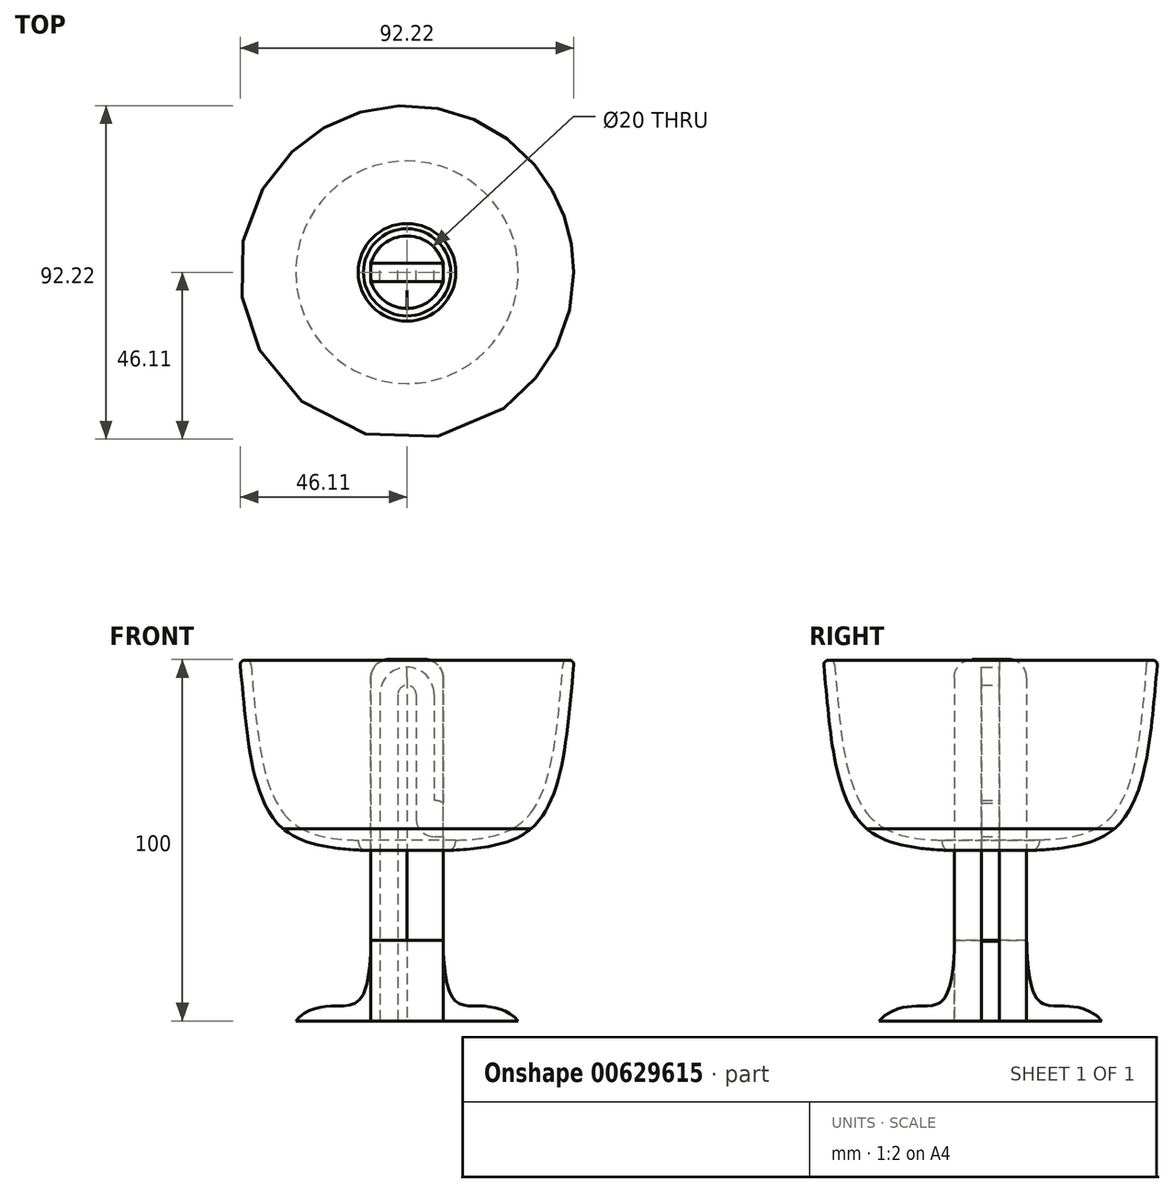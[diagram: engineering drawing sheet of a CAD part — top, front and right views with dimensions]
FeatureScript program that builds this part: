
annotation { "Feature Type Name" : "Feature", "Feature Type Description" : "" }
export const myFeature = defineFeature(function(context is Context, id is Id, definition is map)
    precondition{}
    {
        {
            var Q0;
            Q0=qCreatedBy(makeId("Front.planeOp"),FACE);
            var sketch = newSketch(context, id + "F0", { "sketchPlane" : qUnion([Q0])});
            skLineSegment(sketch, "E0.bottom", {"start": v(10, 50) * mm, "end": v(-10, 50) * mm});
            skLineSegment(sketch, "E0.top", {"start": v(10, -50) * mm, "end": v(-10, -50) * mm});
            skLineSegment(sketch, "E0.left", {"start": v(10, 50) * mm, "end": v(10, -50) * mm});
            skLineSegment(sketch, "E0.right", {"start": v(-10, 50) * mm, "end": v(-10, -50) * mm});
            skPoint(sketch, "E0.middle", {"position": v(0, 0) * mm});
            skLineSegment(sketch, "E1", {"start": v(10, -50) * mm, "end": v(30.79, -50) * mm});
            skFitSpline(sketch, "E2", {"points": [v(30.79, -50) * mm, v(20.87, -45.89) * mm, v(12.34, -43.12) * mm, v(10, -27.67) * mm, v(10, -27.9) * mm], "startDerivative": vector(-25.17, 29.69) * mm, "endDerivative": vector(0.32, -8.68) * mm});
            skFitSpline(sketch, "E3", {"points": [v(10, 0) * mm, v(32.17, 5.3) * mm, v(43.24, 49.8) * mm], "startDerivative": vector(45.4, 0) * mm, "endDerivative": vector(8.68, 94.37) * mm});
            skCircle(sketch, "E4", {"center": v(0, 40.36) * mm, "radius": 2.5 * mm});
            skCircle(sketch, "E5", {"center": v(5, 40.36) * mm, "radius": 2.5 * mm});
            skCircle(sketch, "E6", {"center": v(-5, 40.36) * mm, "radius": 2.5 * mm});
            skCircle(sketch, "E7", {"center": v(0, 40.36) * mm, "radius": 7.5 * mm});
            skLineSegment(sketch, "E8", {"start": v(-2.5, 40.36) * mm, "end": v(-2.5, -50) * mm});
            skLineSegment(sketch, "E9", {"start": v(-7.5, 40.36) * mm, "end": v(-7.5, -50) * mm});
            skLineSegment(sketch, "E10", {"start": v(2.5, 40.36) * mm, "end": v(2.5, 6) * mm});
            skLineSegment(sketch, "E11", {"start": v(7.5, 40.36) * mm, "end": v(7.5, 6) * mm});
            skCircle(sketch, "E12", {"center": v(10, 0) * mm, "radius": 3.5 * mm});
            skCircle(sketch, "E13", {"center": v(10, 6) * mm, "radius": 2.5 * mm});
            skCircle(sketch, "E14", {"center": v(10, 3.5) * mm, "radius": 2.5 * mm});
            skCircle(sketch, "E15", {"center": v(7.5, 6) * mm, "radius": 5 * mm});
            skLineSegment(sketch, "E16", {"start": v(7.5, 1) * mm, "end": v(10, 1) * mm});
            skLineSegment(sketch, "E17", {"start": v(43.24, 49.8) * mm, "end": v(46.24, 49.8) * mm});
            skLineSegment(sketch, "E18", {"start": v(10, 0) * mm, "end": v(10, -3) * mm});
            skCircle(sketch, "E19", {"center": v(32.17, 5.3) * mm, "radius": 3 * mm});
            skFitSpline(sketch, "E20", {"points": [v(10, -3) * mm, v(34.26, 3.16) * mm, v(46.24, 49.8) * mm], "startDerivative": vector(44.42, 4.41) * mm, "endDerivative": vector(9.73, 99.39) * mm});
            skLineSegment(sketch, "E21", {"start": v(0, 40.36) * mm, "end": v(0, -50) * mm});
            skSolve(sketch);
        }
        {
            var Q0;
            {var subQ0=sQuery(id+"F0.wireOp",EDGE,"E17");Q0=makeQuery(id+"F0.imprint","IMPRINT",FACE,{"disambiguationData":[TD([[makeQuery(id+"F0.imprint","IMPRINT",EDGE,{"derivedFrom":subQ0}),-1.0]])]});}
            var Q1;
            {var subQ0=sQuery(id+"F0.wireOp",EDGE,"E19");var subQ1=sQuery(id+"F0.wireOp",EDGE,"E3");var subQ2=makeQuery(id+"F0.imprint","INTERSECT",VERTEX,{"disambiguationData":[OD(0.0)],"derivedFrom":[subQ1,subQ0]});Q1=makeQuery(id+"F0.imprint","IMPRINT",FACE,{"disambiguationData":[TD([[makeQuery(id+"F0.imprint","IMPRINT",EDGE,{"disambiguationData":[TD([[subQ2,-1.0]])],"derivedFrom":subQ1}),-1.0]])]});}
            var Q2;
            {var subQ0=sQuery(id+"F0.wireOp",EDGE,"E12");var subQ1=sQuery(id+"F0.wireOp",EDGE,"E3");var subQ2=makeQuery(id+"F0.imprint","INTERSECT",VERTEX,{"derivedFrom":[subQ1,subQ0]});Q2=makeQuery(id+"F0.imprint","IMPRINT",FACE,{"disambiguationData":[TD([[makeQuery(id+"F0.imprint","IMPRINT",EDGE,{"disambiguationData":[TD([[subQ2,-1.0]])],"derivedFrom":subQ1}),-1.0]])]});}
            var Q3;
            {var subQ0=sQuery(id+"F0.wireOp",EDGE,"E18");Q3=makeQuery(id+"F0.imprint","IMPRINT",FACE,{"disambiguationData":[TD([[makeQuery(id+"F0.imprint","IMPRINT",EDGE,{"derivedFrom":subQ0}),1.0]])]});}
            var Q4;
            {var subQ4=sQuery(id+"F0.wireOp",EDGE,"E1");Q4=makeQuery(id+"F0.imprint","IMPRINT",FACE,{"disambiguationData":[TD([[makeQuery(id+"F0.imprint","IMPRINT",EDGE,{"derivedFrom":subQ4}),1.0]])]});}
            var Q5;
            Q5=sQuery(id+"F0.wireOp",EDGE,"E21");
            revolve(context, id + "F1", {"entities" : qUnion([Q0, Q1, Q2, Q3, Q4]), "axis" : qUnion([Q5]), "revolveType" : RevolveType.FULL});
        }
        {
            var Q0;
            {var subQ1=sQuery(id+"F0.wireOp",EDGE,"E0.left");var subQ6=sQuery(id+"F0.wireOp",EDGE,"E12");var subQ7=makeQuery(id+"F0.imprint","INTERSECT",VERTEX,{"derivedFrom":[subQ1,subQ6]});Q0=makeQuery(id+"F0.imprint","IMPRINT",FACE,{"disambiguationData":[TD([[makeQuery(id+"F0.imprint","IMPRINT",EDGE,{"disambiguationData":[TD([[subQ7,-1.0]])],"derivedFrom":subQ1}),-1.0]])]});}
            var Q1;
            {var subQ2=sQuery(id+"F0.wireOp",EDGE,"E0.bottom");Q1=makeQuery(id+"F0.imprint","IMPRINT",FACE,{"disambiguationData":[TD([[makeQuery(id+"F0.imprint","IMPRINT",EDGE,{"derivedFrom":subQ2}),1.0]])]});}
            var Q2;
            {var subQ0=sQuery(id+"F0.wireOp",EDGE,"E8");var subQ1=sQuery(id+"F0.wireOp",EDGE,"E0.top");var subQ2=makeQuery(id+"F0.imprint","INTERSECT",VERTEX,{"derivedFrom":[subQ1,subQ0]});Q2=makeQuery(id+"F0.imprint","IMPRINT",FACE,{"disambiguationData":[TD([[makeQuery(id+"F0.imprint","IMPRINT",EDGE,{"disambiguationData":[TD([[subQ2,1.0]])],"derivedFrom":subQ1}),-1.0]])]});}
            var Q3;
            {var subQ0=sQuery(id+"F0.wireOp",EDGE,"E8");var subQ5=sQuery(id+"F0.wireOp",EDGE,"E7");var subQ6=makeQuery(id+"F0.imprint","INTERSECT",VERTEX,{"derivedFrom":[subQ5,subQ0]});Q3=makeQuery(id+"F0.imprint","IMPRINT",FACE,{"disambiguationData":[TD([[makeQuery(id+"F0.imprint","IMPRINT",EDGE,{"disambiguationData":[TD([[subQ6,-1.0]])],"derivedFrom":subQ5}),1.0]])]});}
            var Q4;
            {var subQ3=sQuery(id+"F0.wireOp",EDGE,"E21");var subQ5=sQuery(id+"F0.wireOp",EDGE,"E7");var subQ6=makeQuery(id+"F0.imprint","INTERSECT",VERTEX,{"derivedFrom":[subQ5,subQ3]});Q4=makeQuery(id+"F0.imprint","IMPRINT",FACE,{"disambiguationData":[TD([[makeQuery(id+"F0.imprint","IMPRINT",EDGE,{"disambiguationData":[TD([[subQ6,-1.0]])],"derivedFrom":subQ5}),1.0]])]});}
            var Q5;
            {var subQ0=sQuery(id+"F0.wireOp",EDGE,"E4");var subQ3=makeQuery(id+"F0.imprint","INTERSECT",VERTEX,{"derivedFrom":[subQ0,sQuery(id+"F0.wireOp",EDGE,"E21")]});Q5=makeQuery(id+"F0.imprint","IMPRINT",FACE,{"disambiguationData":[TD([[makeQuery(id+"F0.imprint","IMPRINT",EDGE,{"disambiguationData":[TD([[subQ3,1.0]])],"derivedFrom":subQ0}),1.0]])]});}
            var Q6;
            {var subQ0=sQuery(id+"F0.wireOp",EDGE,"E16");Q6=makeQuery(id+"F0.imprint","IMPRINT",FACE,{"disambiguationData":[TD([[makeQuery(id+"F0.imprint","IMPRINT",EDGE,{"derivedFrom":subQ0}),-1.0]])]});}
            extrude(context, id + "F2", {"entities" : qUnion([Q0, Q1, Q2, Q3, Q4, Q5, Q6]), "endBound" : BoundingType.SYMMETRIC, "depth" : 5 * mm, "offsetDistance" : 25 * mm});
        }
        {
            var Q0;
            Q0=makeQuery(id+"F2.opExtrude","CAP_FACE",FACE,{"disambiguationData":[OSD([sQuery(id+"F0.wireOp",EDGE,"E0.bottom"),sQuery(id+"F0.wireOp",EDGE,"E0.top"),sQuery(id+"F0.wireOp",EDGE,"E0.left"),sQuery(id+"F0.wireOp",EDGE,"E0.right"),sQuery(id+"F0.wireOp",EDGE,"E7"),sQuery(id+"F0.wireOp",EDGE,"E9"),sQuery(id+"F0.wireOp",EDGE,"E11"),sQuery(id+"F0.wireOp",EDGE,"E15")])],"isStart":false});
            var sketch = newSketch(context, id + "F3", { "sketchPlane" : qUnion([Q0])});
            skLineSegment(sketch, "E22.bottom", {"start": v(-10, -50) * mm, "end": v(10, -50) * mm});
            skLineSegment(sketch, "E22.top", {"start": v(-10, 50) * mm, "end": v(10, 50) * mm});
            skLineSegment(sketch, "E22.left", {"start": v(-10, -50) * mm, "end": v(-10, 50) * mm});
            skLineSegment(sketch, "E22.right", {"start": v(10, -50) * mm, "end": v(10, 50) * mm});
            skSolve(sketch);
        }
        {
            var Q0;
            Q0 = qSketchRegion(id + "F3", true);
            extrude(context, id + "F4", {"entities" : qUnion([Q0]), "depth" : 7.5 * mm, "offsetDistance" : 25 * mm});
        }
        {
            var Q0;
            Q0=makeQuery(id+"F4.opExtrude","CAP_EDGE",EDGE,{"disambiguationData":[OSD([sQuery(id+"F3.wireOp",EDGE,"E22.left")])],"isStart":false});
            var Q1;
            Q1=makeQuery(id+"F4.opExtrude","CAP_EDGE",EDGE,{"disambiguationData":[OSD([sQuery(id+"F3.wireOp",EDGE,"E22.right")])],"isStart":false});
            fillet(context, id + "F5", {"entities" : qUnion([Q0, Q1]), "radius" : 10.5 * mm, "tangentPropagation" : true, "allowEdgeOverflow" : false});
        }
        {
            var Q0;
            Q0=makeQuery(id+"F2.opExtrude","CAP_FACE",FACE,{"disambiguationData":[OSD([sQuery(id+"F0.wireOp",EDGE,"E0.top"),sQuery(id+"F0.wireOp",EDGE,"E0.left"),sQuery(id+"F0.wireOp",EDGE,"E2"),sQuery(id+"F0.wireOp",EDGE,"E4"),sQuery(id+"F0.wireOp",EDGE,"E8"),sQuery(id+"F0.wireOp",EDGE,"E10"),sQuery(id+"F0.wireOp",EDGE,"E15"),sQuery(id+"F0.wireOp",EDGE,"E16"),sQuery(id+"F0.wireOp",EDGE,"E18")])],"isStart":true});
            var sketch = newSketch(context, id + "F6", { "sketchPlane" : qUnion([Q0])});
            skLineSegment(sketch, "E23.bottom", {"start": v(-10, -50) * mm, "end": v(10, -50) * mm});
            skLineSegment(sketch, "E23.top", {"start": v(-10, 50) * mm, "end": v(10, 50) * mm});
            skLineSegment(sketch, "E23.left", {"start": v(-10, -50) * mm, "end": v(-10, 50) * mm});
            skLineSegment(sketch, "E23.right", {"start": v(10, -50) * mm, "end": v(10, 50) * mm});
            skSolve(sketch);
        }
        {
            var Q0;
            Q0 = qSketchRegion(id + "F6", true);
            extrude(context, id + "F7", {"entities" : qUnion([Q0]), "depth" : 7.5 * mm, "offsetDistance" : 25 * mm});
        }
        {
            var Q0;
            Q0=makeQuery(id+"F7.opExtrude","CAP_EDGE",EDGE,{"disambiguationData":[OSD([sQuery(id+"F6.wireOp",EDGE,"E23.left")])],"isStart":false});
            var Q1;
            Q1=makeQuery(id+"F7.opExtrude","CAP_EDGE",EDGE,{"disambiguationData":[OSD([sQuery(id+"F6.wireOp",EDGE,"E23.right")])],"isStart":false});
            fillet(context, id + "F8", {"entities" : qUnion([Q0, Q1]), "radius" : 10 * mm, "tangentPropagation" : true, "allowEdgeOverflow" : false});
        }
        {
            var Q0;
            Q0=makeQuery(id+"F8.opFillet","BLEND_EDGE",EDGE,{"blendedFrom":[makeQuery(id+"F7.opExtrude","CAP_EDGE",EDGE,{"disambiguationData":[OSD([sQuery(id+"F6.wireOp",EDGE,"E23.left")])],"isStart":false}),makeQuery(id+"F7.opExtrude","SWEPT_FACE",FACE,{"disambiguationData":[OSD([sQuery(id+"F6.wireOp",EDGE,"E23.top")])]})],"blendedInto":[makeQuery(id+"F7.opExtrude","SWEPT_FACE",FACE,{"disambiguationData":[OSD([sQuery(id+"F6.wireOp",EDGE,"E23.top")])]})]});
            var Q1;
            Q1=makeQuery(id+"F8.opFillet","BLEND_EDGE",EDGE,{"blendedFrom":[makeQuery(id+"F7.opExtrude","CAP_EDGE",EDGE,{"disambiguationData":[OSD([sQuery(id+"F6.wireOp",EDGE,"E23.right")])],"isStart":false}),makeQuery(id+"F7.opExtrude","SWEPT_FACE",FACE,{"disambiguationData":[OSD([sQuery(id+"F6.wireOp",EDGE,"E23.top")])]})],"blendedInto":[makeQuery(id+"F7.opExtrude","SWEPT_FACE",FACE,{"disambiguationData":[OSD([sQuery(id+"F6.wireOp",EDGE,"E23.top")])]})]});
            var Q2;
            Q2=makeQuery(id+"F2.opExtrude","SWEPT_EDGE",EDGE,{"disambiguationData":[OSD([sQuery(id+"F0.wireOp",EDGE,"E0.bottom"),sQuery(id+"F0.wireOp",EDGE,"E0.left")])]});
            var Q3;
            Q3=makeQuery(id+"F5.opFillet","BLEND_EDGE",EDGE,{"blendedFrom":[makeQuery(id+"F4.opExtrude","CAP_EDGE",EDGE,{"disambiguationData":[OSD([sQuery(id+"F3.wireOp",EDGE,"E22.right")])],"isStart":false}),makeQuery(id+"F4.opExtrude","SWEPT_FACE",FACE,{"disambiguationData":[OSD([sQuery(id+"F3.wireOp",EDGE,"E22.top")])]})],"blendedInto":[makeQuery(id+"F4.opExtrude","SWEPT_FACE",FACE,{"disambiguationData":[OSD([sQuery(id+"F3.wireOp",EDGE,"E22.top")])]})]});
            var Q4;
            Q4=makeQuery(id+"F5.opFillet","BLEND_EDGE",EDGE,{"blendedFrom":[makeQuery(id+"F4.opExtrude","CAP_EDGE",EDGE,{"disambiguationData":[OSD([sQuery(id+"F3.wireOp",EDGE,"E22.left")])],"isStart":false}),makeQuery(id+"F4.opExtrude","SWEPT_FACE",FACE,{"disambiguationData":[OSD([sQuery(id+"F3.wireOp",EDGE,"E22.top")])]})],"blendedInto":[makeQuery(id+"F4.opExtrude","SWEPT_FACE",FACE,{"disambiguationData":[OSD([sQuery(id+"F3.wireOp",EDGE,"E22.top")])]})]});
            var Q5;
            Q5=makeQuery(id+"F2.opExtrude","SWEPT_EDGE",EDGE,{"disambiguationData":[OSD([sQuery(id+"F0.wireOp",EDGE,"E0.bottom"),sQuery(id+"F0.wireOp",EDGE,"E0.right")])]});
            fillet(context, id + "F9", {"entities" : qUnion([Q0, Q1, Q2, Q3, Q4, Q5]), "radius" : 5 * mm, "tangentPropagation" : true, "allowEdgeOverflow" : false});
        }
        {
            var Q0;
            Q0=makeQuery(id+"F1.opRevolve","SWEPT_EDGE",EDGE,{"disambiguationData":[OSD([sQuery(id+"F0.wireOp",EDGE,"E17"),sQuery(id+"F0.wireOp",EDGE,"E20")])]});
            var Q1;
            Q1=makeQuery(id+"F1.opRevolve","SWEPT_EDGE",EDGE,{"disambiguationData":[OSD([sQuery(id+"F0.wireOp",EDGE,"E3"),sQuery(id+"F0.wireOp",EDGE,"E17")])]});
            fillet(context, id + "F10", {"entities" : qUnion([Q0, Q1]), "radius" : 1.25 * mm, "tangentPropagation" : true, "allowEdgeOverflow" : false});
        }
    });
